# Revit family: A2W_HWT_4-6_Outdoor Unit
name_source: partatom
category: Mechanical Equipment
revit_build: Autodesk Revit 2017 (Build: 20160225_1515(x64)
units: mm (PartAtom-declared; Revit-internal decimal feet)

## family parameters
Always vertical = Yes
Cut with Voids When Loaded = No
OmniClass Number = 23.75.00.00
OmniClass Title = Climate Control (HVAC)
Part Type = Normal
Room Calculation Point = No
Round Connector Dimension = Use Diameter
Shared = No
Work Plane-Based = No

## types (2) — shared parameters
Article Description = ESTIA R32
Back up heater capacity kW = -
Compressor detail - Motor output  (W) = 1100
Compressor detail - Type = Hermetic DC rotary compressor
Content Supplier URL = www.hcltech.com
Custom = No
Depth (mm) = 300 mm
Description = ESTIA R32
Drain piping diameter (mm) = -
EMCS = 4
ETIM Article Class = EC001213
Energy efficiency class - Low temp. = A+++
Frequency (Hz) = 50Hz
Height (mm) = 630 mm  [stored 2.06693 ft]
Hydronic Return Diameter (mm) = 13 mm
Hydronic Supply Diameter (mm) = 6 mm  [stored 0.019685 ft]
MCA = -
MEPcontent Class = HEATPUMP
MOCP = 16
Manufacturer = Toshiba
Manufacturer URL = https://www.toshiba-carrier.co.jp
Maximum current A = 14.6
Operating range - Cooling (°C) = 10 - 43
Operating range - Heating (°C) = -20 - 25
Operating range - Hot Water (°C) = -20 - 43
Power consumption-Cooling (Kw) = -
Power consumption-Heating (Kw) = -
Product Line = TCAE
Red = Colour RGB-255 000 000
Refrigerant information = R32
Running current-Cooling (A) = -
Running current-Heating (A) = -
Sound Power level (dB(A))-Cooling/Heating = 62 / 65
URL = https://www.toshiba-carrier.co.jp
Voltage (V) = 220-240
Water Piping diameter-Inlet/Outlet (mm) = -
Weight (Kg) = 42
White = Colour RGB-255 255 255
Width (mm) = 800 mm  [stored 2.62467 ft]

## per-type parameters (varying)
| type | Rated Capacity kW-Cooling/Heating | Rated Power Consumption kW-Cooling/Heating | Rated efficiency-EER / COP | Rated water flow rate -L/min | Seasonal space heating energy efficiency (ηs) |
| HWT-401WH-E | 4.0 / 4.0 | 1.15/0.77 | 3.45 / 5.20 | 11.5/11.6 | 178% |
| HWT-601WH-E | 5.0 / 6.0 | 1.52/1.25 | 3.30 / 4.80 | - | 180% |

note: column(s) folded — value = type name in every type: Article Type, Manufacturer Art. No., Model

note: [stored X ft] marks values corroborated as IEEE doubles in the binary element streams (Revit-internal decimal feet)

## geometry (parser evidence)
native form markers: Sweep x9
no freeform markers — native parametric forms only
